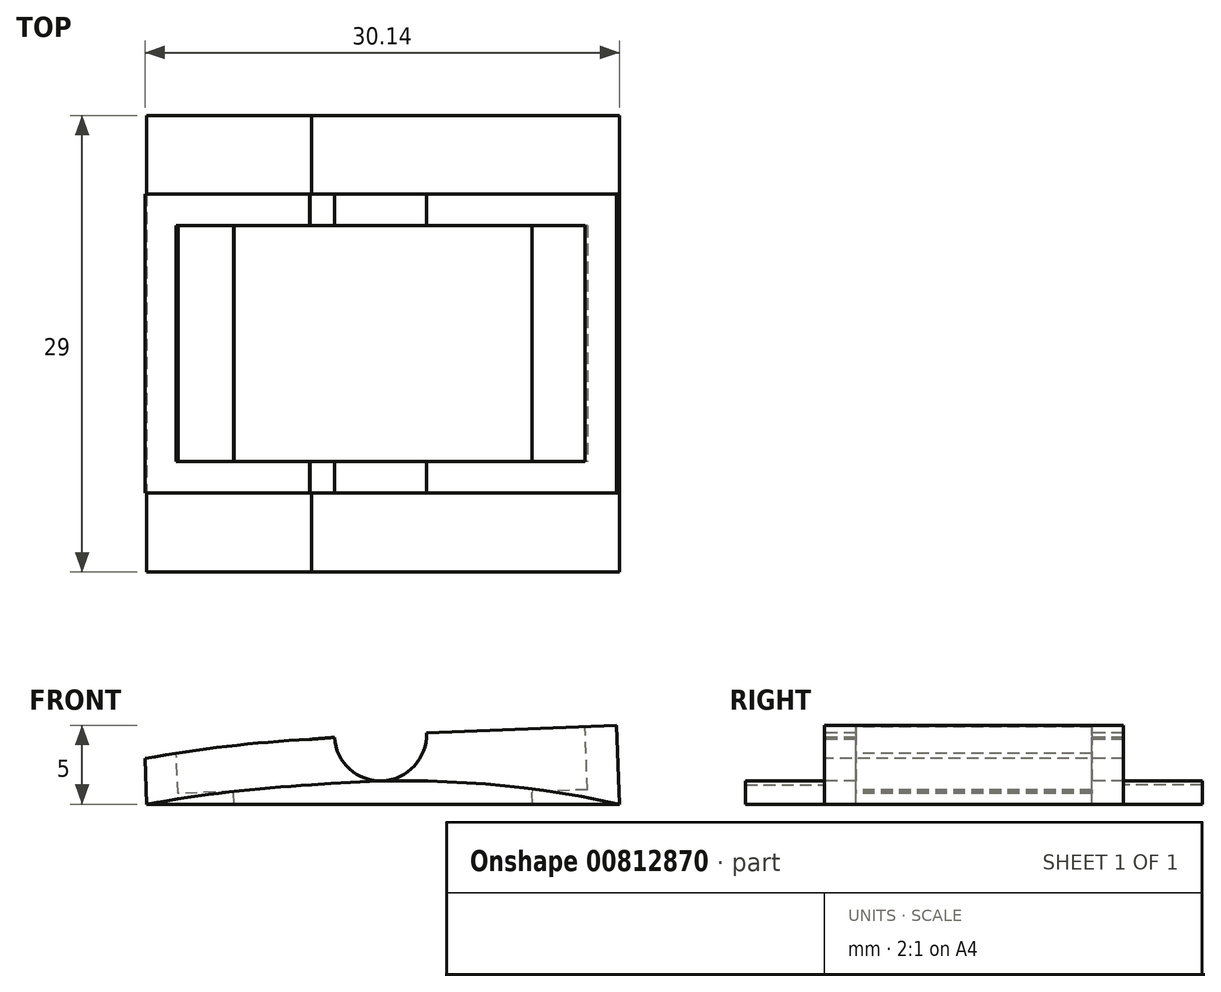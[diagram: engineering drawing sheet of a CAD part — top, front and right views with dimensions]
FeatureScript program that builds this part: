
annotation { "Feature Type Name" : "Feature", "Feature Type Description" : "" }
export const myFeature = defineFeature(function(context is Context, id is Id, definition is map)
    precondition{}
    {
        {
            var Q0;
            Q0=qCreatedBy(makeId("Top.planeOp"),FACE);
            var sketch = newSketch(context, id + "F0", { "sketchPlane" : qUnion([Q0])});
            skLineSegment(sketch, "E0.bottom", {"start": v(15, 14.5) * mm, "end": v(-15, 14.5) * mm});
            skLineSegment(sketch, "E0.top", {"start": v(15, -14.5) * mm, "end": v(-15, -14.5) * mm});
            skLineSegment(sketch, "E0.left", {"start": v(15, 14.5) * mm, "end": v(15, -14.5) * mm});
            skLineSegment(sketch, "E0.right", {"start": v(-15, 14.5) * mm, "end": v(-15, -14.5) * mm});
            skPoint(sketch, "E0.middle", {"position": v(0, 0) * mm});
            skLineSegment(sketch, "E1", {"start": v(-15, 9.5) * mm, "end": v(15, 9.5) * mm});
            skLineSegment(sketch, "E2.MirrorCS", {"start": v(-15, -9.5) * mm, "end": v(15, -9.5) * mm});
            skSolve(sketch);
        }
        {
            var Q0;
            {var subQ0=sQuery(id+"F0.wireOp",EDGE,"E1");Q0=makeQuery(id+"F0.imprint","IMPRINT",FACE,{"disambiguationData":[TD([[makeQuery(id+"F0.imprint","IMPRINT",EDGE,{"derivedFrom":subQ0}),-1.0]])]});}
            extrude(context, id + "F1", {"entities" : qUnion([Q0]), "depth" : 5 * mm, "offsetDistance" : 25 * mm});
        }
        {
            var Q0;
            Q0=makeQuery(id+"F1.opExtrude","SWEPT_FACE",FACE,{"disambiguationData":[OSD([sQuery(id+"F0.wireOp",EDGE,"E2.MirrorCS")])]});
            var sketch = newSketch(context, id + "F2", { "sketchPlane" : qUnion([Q0])});
            skArc(sketch, "E3", {"start": v(15, 0) * mm, "mid": v(5.33, 1.75) * mm, "end": v(-4.49, 2) * mm});
            skLineSegment(sketch, "E4", {"start": v(-15, 0) * mm, "end": v(15, 0) * mm});
            skLineSegment(sketch, "E5", {"start": v(-15, 0) * mm, "end": v(-15, 1.2) * mm});
            skArc(sketch, "E6", {"start": v(-4.49, 2) * mm, "mid": v(-9.76, 1.77) * mm, "end": v(-15, 1.2) * mm});
            skSolve(sketch);
        }
        {
            var Q0;
            Q0=makeQuery(id+"F2.imprint","IMPRINT",FACE,{"disambiguationData":[TD([[makeQuery(id+"F2.imprint","IMPRINT",EDGE,{"derivedFrom":sQuery(id+"F2.wireOp",EDGE,"E3")}),1.0]])]});
            extrude(context, id + "F3", {"entities" : qUnion([Q0]), "operationType" : NewBodyOperationType.ADD, "depth" : 5 * mm, "offsetDistance" : 25 * mm});
        }
        {
            var Q0;
            Q0=makeQuery(id+"F3.opExtrude","CAP_FACE",FACE,{"disambiguationData":[OSD([sQuery(id+"F2.wireOp",EDGE,"E3"),sQuery(id+"F2.wireOp",EDGE,"TGZ4EUM7-mO86-7CJG-3V2t-0yu6nJWBbOyP"),sQuery(id+"F2.wireOp",EDGE,"E4")])],"isStart":false});
            extrude(context, id + "F4", {"entities" : qUnion([Q0]), "operationType" : NewBodyOperationType.ADD, "oppositeDirection" : true, "depth" : 29 * mm, "offsetDistance" : 25 * mm});
        }
        {
            var Q0;
            Q0=makeQuery(id+"F1.opExtrude","CAP_FACE",FACE,{"disambiguationData":[OSD([sQuery(id+"F0.wireOp",EDGE,"E0.left"),sQuery(id+"F0.wireOp",EDGE,"E0.right"),sQuery(id+"F0.wireOp",EDGE,"E1"),sQuery(id+"F0.wireOp",EDGE,"E2.MirrorCS")])],"isStart":false});
            var sketch = newSketch(context, id + "F5", { "sketchPlane" : qUnion([Q0])});
            skLineSegment(sketch, "E7.bottom", {"start": v(13, 7.5) * mm, "end": v(-13, 7.5) * mm});
            skLineSegment(sketch, "E7.top", {"start": v(13, -7.5) * mm, "end": v(-13, -7.5) * mm});
            skLineSegment(sketch, "E7.left", {"start": v(13, 7.5) * mm, "end": v(13, -7.5) * mm});
            skLineSegment(sketch, "E7.right", {"start": v(-13, 7.5) * mm, "end": v(-13, -7.5) * mm});
            skPoint(sketch, "E7.middle", {"position": v(0, 0) * mm});
            skSolve(sketch);
        }
        {
            var Q0;
            Q0=makeQuery(id+"F5.imprint","IMPRINT",FACE,{"disambiguationData":[TD([[makeQuery(id+"F5.imprint","IMPRINT",EDGE,{"derivedFrom":sQuery(id+"F5.wireOp",EDGE,"E7.bottom")}),1.0]])]});
            extrude(context, id + "F6", {"entities" : qUnion([Q0]), "operationType" : NewBodyOperationType.REMOVE, "oppositeDirection" : true, "depth" : 4 * mm, "offsetDistance" : 25 * mm});
        }
        {
            var Q0;
            Q0=makeQuery(id+"F6.boolean.opBoolean","COPY",FACE,{"derivedFrom":makeQuery(id+"F6.opExtrude","CAP_FACE",FACE,{"disambiguationData":[OSD([sQuery(id+"F5.wireOp",EDGE,"E7.bottom"),sQuery(id+"F5.wireOp",EDGE,"E7.top"),sQuery(id+"F5.wireOp",EDGE,"E7.left"),sQuery(id+"F5.wireOp",EDGE,"E7.right")])],"isStart":false})});
            var sketch = newSketch(context, id + "F7", { "sketchPlane" : qUnion([Q0])});
            skLineSegment(sketch, "E8.bottom", {"start": v(9.47, 7.5) * mm, "end": v(-9.47, 7.5) * mm});
            skLineSegment(sketch, "E8.top", {"start": v(9.47, -7.5) * mm, "end": v(-9.47, -7.5) * mm});
            skLineSegment(sketch, "E8.left", {"start": v(9.47, 7.5) * mm, "end": v(9.47, -7.5) * mm});
            skLineSegment(sketch, "E8.right", {"start": v(-9.47, 7.5) * mm, "end": v(-9.47, -7.5) * mm});
            skPoint(sketch, "E8.middle", {"position": v(0, 0) * mm});
            skSolve(sketch);
        }
        {
            var Q0;
            Q0=makeQuery(id+"F7.imprint","IMPRINT",FACE,{"disambiguationData":[TD([[makeQuery(id+"F7.imprint","IMPRINT",EDGE,{"derivedFrom":sQuery(id+"F7.wireOp",EDGE,"E8.bottom")}),1.0]])]});
            extrude(context, id + "F8", {"entities" : qUnion([Q0]), "operationType" : NewBodyOperationType.REMOVE, "oppositeDirection" : true, "depth" : 25 * mm, "offsetDistance" : 25 * mm});
        }
        {
            var Q0;
            Q0=makeQuery(id+"F1.opExtrude","SWEPT_FACE",FACE,{"disambiguationData":[OSD([sQuery(id+"F0.wireOp",EDGE,"E2.MirrorCS")])]});
            var sketch = newSketch(context, id + "F9", { "sketchPlane" : qUnion([Q0])});
            skCircle(sketch, "E9", {"center": v(0, 5) * mm, "radius": 2.92 * mm});
            skSolve(sketch);
        }
        {
            var Q0;
            {var subQ0=sQuery(id+"F9.wireOp",EDGE,"E9");var subQ1=makeQuery(id+"F1.opExtrude","CAP_EDGE",EDGE,{"disambiguationData":[OSD([sQuery(id+"F0.wireOp",EDGE,"E2.MirrorCS")])],"isStart":false});var subQ2=makeQuery(id+"F9.imprint","INTERSECT",VERTEX,{"disambiguationData":[OD(0.0)],"derivedFrom":[subQ1,subQ0]});Q0=makeQuery(id+"F9.imprint","IMPRINT",FACE,{"disambiguationData":[TD([[makeQuery(id+"F9.imprint","IMPRINT",EDGE,{"disambiguationData":[TD([[subQ2,-1.0]])],"derivedFrom":subQ0}),1.0]])]});}
            extrude(context, id + "F10", {"entities" : qUnion([Q0]), "operationType" : NewBodyOperationType.REMOVE, "oppositeDirection" : true, "depth" : 25 * mm, "offsetDistance" : 25 * mm});
        }
        {
            var Q0;
            {var subQ0=sQuery(id+"F0.wireOp",EDGE,"E2.MirrorCS");var subQ1=makeQuery(id+"F1.opExtrude","SWEPT_FACE",FACE,{"disambiguationData":[OSD([subQ0])]});var subQ3=sQuery(id+"F0.wireOp",EDGE,"E0.right");Q0=makeQuery(id+"F10.boolean.opBoolean","SPLIT",FACE,{"disambiguationData":[TD([makeQuery(id+"F1.opExtrude","SWEPT_FACE",FACE,{"disambiguationData":[OSD([subQ3])]})])],"derivedFrom":subQ1});}
            var sketch = newSketch(context, id + "F11", { "sketchPlane" : qUnion([Q0])});
            skArc(sketch, "E10.0", {"start": v(-4.49, 2) * mm, "mid": v(-9.76, 1.77) * mm, "end": v(-15, 1.2) * mm});
            skArc(sketch, "E10.1", {"start": v(15, 0) * mm, "mid": v(5.33, 1.75) * mm, "end": v(-4.49, 2) * mm});
            skArc(sketch, "E11.0", {"start": v(-4.49, 4.9) * mm, "mid": v(-9.76, 4.67) * mm, "end": v(-15, 4.1) * mm});
            skArc(sketch, "E11.1", {"start": v(15, 2.9) * mm, "mid": v(5.33, 4.65) * mm, "end": v(-4.49, 4.9) * mm});
            skLineSegment(sketch, "E12", {"start": v(-15, 4.1) * mm, "end": v(-15, 6.88) * mm});
            skLineSegment(sketch, "E13", {"start": v(-15, 6.88) * mm, "end": v(15, 6.88) * mm});
            skLineSegment(sketch, "E14", {"start": v(15, 6.88) * mm, "end": v(15, 2.9) * mm});
            skSolve(sketch);
        }
        {
            var Q0;
            {var subQ5=sQuery(id+"F11.wireOp",EDGE,"E11.1");var subQ6=sQuery(id+"F11.wireOp",EDGE,"E11.0");var subQ7=makeQuery(id+"F11.imprint","INTERSECT",VERTEX,{"derivedFrom":[subQ6,subQ5]});Q0=makeQuery(id+"F11.imprint","IMPRINT",FACE,{"disambiguationData":[TD([[makeQuery(id+"F11.imprint","IMPRINT",EDGE,{"disambiguationData":[TD([[subQ7,1.0]])],"derivedFrom":subQ5}),-1.0]])]});}
            var Q1;
            {var subQ0=sQuery(id+"F11.wireOp",EDGE,"E12");Q1=makeQuery(id+"F11.imprint","IMPRINT",FACE,{"disambiguationData":[TD([[makeQuery(id+"F11.imprint","IMPRINT",EDGE,{"derivedFrom":subQ0}),-1.0]])]});}
            extrude(context, id + "F12", {"entities" : qUnion([Q0, Q1]), "operationType" : NewBodyOperationType.REMOVE, "oppositeDirection" : true, "depth" : 25 * mm, "offsetDistance" : 25 * mm});
        }
        {
            var Q0;
            Q0=makeQuery(id+"F12.boolean.opBoolean","COPY",EDGE,{"derivedFrom":makeQuery(id+"F12.opExtrude","SWEPT_EDGE",EDGE,{"disambiguationData":[OSD([sQuery(id+"F11.wireOp",EDGE,"E11.1"),sQuery(id+"F11.wireOp",EDGE,"E14")])]})});
            var Q1;
            Q1=makeQuery(id+"F12.boolean.opBoolean","COPY",EDGE,{"derivedFrom":makeQuery(id+"F12.opExtrude","SWEPT_EDGE",EDGE,{"disambiguationData":[OSD([sQuery(id+"F0.wireOp",EDGE,"E0.right"),sQuery(id+"F0.wireOp",EDGE,"E2.MirrorCS"),sQuery(id+"F11.wireOp",EDGE,"E11.0"),sQuery(id+"F11.wireOp",EDGE,"E12")])]})});
            chamfer(context, id + "F13", {"entities" : qUnion([Q0, Q1]), "width" : 1 * mm, "tangentPropagation" : true});
        }
        {
            var Q0;
            Q0=makeQuery(id+"F3.opExtrude","CAP_FACE",FACE,{"disambiguationData":[OSD([sQuery(id+"F2.wireOp",EDGE,"E3"),sQuery(id+"F2.wireOp",EDGE,"E4"),sQuery(id+"F2.wireOp",EDGE,"E5"),sQuery(id+"F2.wireOp",EDGE,"E6")])],"isStart":false});
            var sketch = newSketch(context, id + "F14", { "sketchPlane" : qUnion([Q0])});
            skLineSegment(sketch, "E15", {"start": v(15, 0) * mm, "end": v(-15, 1.2) * mm});
            skSolve(sketch);
        }
        {
            var Q0;
            {var subQ0=sQuery(id+"F5.wireOp",EDGE,"E7.right");var subQ1=sQuery(id+"F5.wireOp",EDGE,"E7.top");var subQ2=sQuery(id+"F5.wireOp",EDGE,"E7.bottom");Q0=makeQuery(id+"F8.boolean.opBoolean","SPLIT",FACE,{"disambiguationData":[TD([makeQuery(id+"F6.boolean.opBoolean","COPY",FACE,{"derivedFrom":makeQuery(id+"F6.opExtrude","SWEPT_FACE",FACE,{"disambiguationData":[OSD([subQ0])]})})])],"derivedFrom":makeQuery(id+"F6.boolean.opBoolean","COPY",FACE,{"derivedFrom":makeQuery(id+"F6.opExtrude","CAP_FACE",FACE,{"disambiguationData":[OSD([subQ2,subQ1,sQuery(id+"F5.wireOp",EDGE,"E7.left"),subQ0])],"isStart":false})})});}
            extrude(context, id + "F15", {"entities" : qUnion([Q0]), "operationType" : NewBodyOperationType.ADD, "depth" : 1 * mm, "offsetDistance" : 25 * mm});
        }
        {
            var Q0;
            Q0=makeQuery(id+"F14.imprint","IMPRINT",FACE,{"disambiguationData":[TD([[makeQuery(id+"F14.imprint","IMPRINT",EDGE,{"derivedFrom":sQuery(id+"F14.wireOp",EDGE,"E15")}),1.0]])]});
            extrude(context, id + "F16", {"entities" : qUnion([Q0]), "operationType" : NewBodyOperationType.REMOVE, "oppositeDirection" : true, "depth" : 29 * mm, "offsetDistance" : 25 * mm});
        }
        {
            var Q0;
            Q0=makeQuery(id+"F3.opExtrude","CAP_FACE",FACE,{"disambiguationData":[OSD([sQuery(id+"F2.wireOp",EDGE,"E3"),sQuery(id+"F2.wireOp",EDGE,"E4"),sQuery(id+"F2.wireOp",EDGE,"E5"),sQuery(id+"F2.wireOp",EDGE,"E6")])],"isStart":false});
            var sketch = newSketch(context, id + "F17", { "sketchPlane" : qUnion([Q0])});
            skCircle(sketch, "E16", {"center": v(15, 0) * mm, "radius": 1.96 * mm});
            skSolve(sketch);
        }
        {
            var Q0;
            Q0=makeQuery(id+"F1.opExtrude","SWEPT_BODY",BODY,{"disambiguationData":[OSD([sQuery(id+"F0.wireOp",EDGE,"E0.left"),sQuery(id+"F0.wireOp",EDGE,"E0.right"),sQuery(id+"F0.wireOp",EDGE,"E1"),sQuery(id+"F0.wireOp",EDGE,"E2.MirrorCS")])]});
            var Q1;
            Q1=sQuery(id+"F17.wireOp",EDGE,"E16");
            transform(context, id + "F18", {"entities" : qUnion([Q0]), "transformType" : TransformType.ROTATION, "transformAxis" : qUnion([Q1]), "angle" : 2.3 * degree, "makeCopy" : false});
        }
        {
            var Q0;
            Q0=makeQuery(id+"F15.opExtrude","CAP_FACE",FACE,{"disambiguationData":[OSD([sQuery(id+"F5.wireOp",EDGE,"E7.bottom"),sQuery(id+"F5.wireOp",EDGE,"E7.top"),sQuery(id+"F5.wireOp",EDGE,"E7.left"),sQuery(id+"F5.wireOp",EDGE,"E7.right")])],"isStart":false});
            extrude(context, id + "F19", {"entities" : qUnion([Q0]), "operationType" : NewBodyOperationType.REMOVE, "oppositeDirection" : true, "depth" : 0.2 * mm, "offsetDistance" : 25 * mm});
        }
    });
